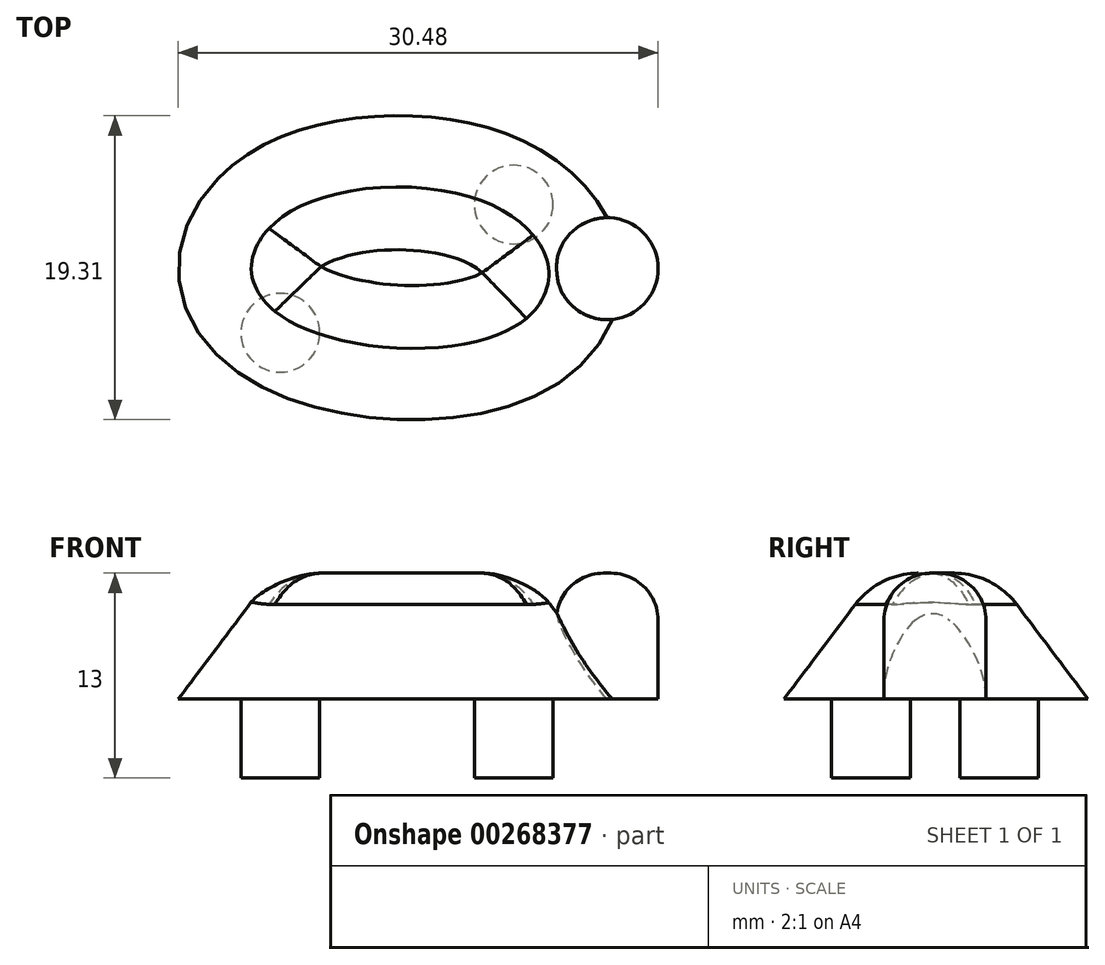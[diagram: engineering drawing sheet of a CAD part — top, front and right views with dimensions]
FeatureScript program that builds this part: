
annotation { "Feature Type Name" : "Feature", "Feature Type Description" : "" }
export const myFeature = defineFeature(function(context is Context, id is Id, definition is map)
    precondition{}
    {
        {
            var Q0;
            Q0=qCreatedBy(makeId("Top.planeOp"),FACE);
            cPlane(context, id + "F0", {"entities" : qUnion([Q0]), "cplaneType" : CPlaneType.OFFSET, "offset" : 5 * mm, "width" : 150 * mm, "height" : 150 * mm});
        }
        {
            var Q0;
            Q0=qCreatedBy(id+"F0.planeOp",FACE);
            var sketch = newSketch(context, id + "F1", { "sketchPlane" : qUnion([Q0])});
            skFitSpline(sketch, "E0", {"points": [v(-8.49, 7.85) * mm, v(-13.9, 0) * mm, v(-8.49, -7.58) * mm, v(8.87, -8.05) * mm, v(14.25, 0) * mm, v(7.82, 8.2) * mm, v(-8.49, 7.85) * mm]});
            skSolve(sketch);
        }
        {
            var Q0;
            Q0 = qSketchRegion(id + "F1", true);
            extrude(context, id + "F2", {"entities" : qUnion([Q0]), "depth" : 8 * mm, "hasDraft" : true, "draftAngle" : 37 * degree, "draftPullDirection" : true});
        }
        {
            var Q0;
            Q0=makeQuery(id+"F2.opExtrude","CAP_EDGE",EDGE,{"disambiguationData":[OSD([sQuery(id+"F1.wireOp",EDGE,"E0")])],"isStart":false});
            fillet(context, id + "F3", {"entities" : qUnion([Q0]), "radius" : 5 * mm, "tangentPropagation" : true, "allowEdgeOverflow" : false});
        }
        {
            var Q0;
            Q0=qCreatedBy(id+"F0.planeOp",FACE);
            var sketch = newSketch(context, id + "F4", { "sketchPlane" : qUnion([Q0])});
            skCircle(sketch, "E1", {"center": v(-7.4, -4.07) * mm, "radius": 2.5 * mm});
            skCircle(sketch, "E2.MirrorC", {"center": v(-7.4, 4.07) * mm, "radius": 2.5 * mm});
            skCircle(sketch, "E3.MirrorC", {"center": v(7.4, -4.07) * mm, "radius": 2.5 * mm});
            skCircle(sketch, "E4.MirrorC", {"center": v(7.4, 4.07) * mm, "radius": 2.5 * mm});
            skSolve(sketch);
        }
        {
            var Q0;
            Q0=qCreatedBy(id+"F0.planeOp",FACE);
            var sketch = newSketch(context, id + "F5", { "sketchPlane" : qUnion([Q0])});
            skCircle(sketch, "E5", {"center": v(13.34, 0) * mm, "radius": 3.24 * mm});
            skSolve(sketch);
        }
        {
            var Q0;
            Q0=makeQuery(id+"F5.imprint","IMPRINT",FACE,{"disambiguationData":[TD([[makeQuery(id+"F5.imprint","IMPRINT",EDGE,{"derivedFrom":sQuery(id+"F5.wireOp",EDGE,"E5")}),1.0]])]});
            extrude(context, id + "F6", {"entities" : qUnion([Q0]), "operationType" : NewBodyOperationType.ADD, "depth" : 8 * mm});
        }
        {
            var Q0;
            Q0=makeQuery(id+"F6.opExtrude","CAP_EDGE",EDGE,{"disambiguationData":[OSD([sQuery(id+"F5.wireOp",EDGE,"E5")])],"isStart":false});
            fillet(context, id + "F7", {"entities" : qUnion([Q0]), "radius" : 3 * mm, "tangentPropagation" : true, "allowEdgeOverflow" : false});
        }
        {
            var Q0;
            Q0=makeQuery(id+"F4.imprint","IMPRINT",FACE,{"disambiguationData":[TD([[makeQuery(id+"F4.imprint","IMPRINT",EDGE,{"derivedFrom":sQuery(id+"F4.wireOp",EDGE,"E3.MirrorC")}),-1.0]])]});
            var Q1;
            Q1=makeQuery(id+"F4.imprint","IMPRINT",FACE,{"disambiguationData":[TD([[makeQuery(id+"F4.imprint","IMPRINT",EDGE,{"derivedFrom":sQuery(id+"F4.wireOp",EDGE,"E4.MirrorC")}),1.0]])]});
            var Q2;
            Q2=makeQuery(id+"F4.imprint","IMPRINT",FACE,{"disambiguationData":[TD([[makeQuery(id+"F4.imprint","IMPRINT",EDGE,{"derivedFrom":sQuery(id+"F4.wireOp",EDGE,"E2.MirrorC")}),-1.0]])]});
            var Q3;
            Q3=makeQuery(id+"F4.imprint","IMPRINT",FACE,{"disambiguationData":[TD([[makeQuery(id+"F4.imprint","IMPRINT",EDGE,{"derivedFrom":sQuery(id+"F4.wireOp",EDGE,"E1")}),1.0]])]});
            extrude(context, id + "F8", {"entities" : qUnion([Q0, Q1, Q2, Q3]), "operationType" : NewBodyOperationType.ADD, "oppositeDirection" : true, "depth" : 5 * mm});
        }
    });
